# Revit family: EFF1_63_UN_Spot_ETK
name_source: partatom
category: Lighting Fixtures
units: mm (PartAtom-declared; Revit-internal decimal feet)

## family parameters
Always vertical = Yes
Cut with Voids When Loaded = Yes
Light Source = No
OmniClass Number = 23.80.70.11.14.11
OmniClass Title = Downlights
Part Type = Normal
Room Calculation Point = Yes
Round Connector Dimension = Use Diameter
Shared = No
Work Plane-Based = No

## types (12) — shared parameters
Assembly Code = 63.0
Bundle = 40°
IfcExportAs = IfcLightFixtureType
IfcExportType = USERDEFINED
Lamp = LED
Manufacturer = ETK licht B.V.
Material = RAL 9003
Model = EFF.1
URL = https://www.etk.nl
Voltage = 230 V

## per-type parameters (varying)
| type | Apparent Load | Light Source | Wattage Comments |
| EFF.1300.15 - 12W / 1500lm / 3000K | 12 VA | EFF.1 - Lightsource : EFF.1300.15 - 12W / 1500lm / 3000K | 12W |
| EFF.1500.15 - 12W / 1550lm / 4000K | 12 VA | EFF.1 - Lightsource : EFF.1500.15 - 12W / 1550lm / 4000K | 12W |
| EFF.1700.15 - 19W / 2400lm / 3000K | 12 VA | EFF.1 - Lightsource : EFF.1700.15 - 19W / 2400lm / 3000K | 12W |
| EFF.1900.15 - 19W / 2500lm / 4000K | 19 VA | EFF.1 - Lightsource : EFF.1900.15 - 19W / 2500lm / 4000K | 19W |
| EFF.1920.15 - 31W / 3550lm / 3000K | 31 VA | EFF.1 - Lightsource : EFF.1920.15 - 31W / 3550lm / 3000K | 31W |
| EFF.1940.15 - 31W / 3650lm / 4000K | 31 VA | EFF.1 - Lightsource : EFF.1940.15 - 31W / 3650lm / 4000K | 31W |
| EFF.1303.15 - 12W / 1500lm / 3000K | 12 VA | EFF.1 - Lightsource : EFF.1303.15 - 12W / 1500lm / 3000K | 12W |
| EFF.1503.15 - 12W / 1550lm / 4000K | 12 VA | EFF.1 - Lightsource : EFF.1503.15 - 12W / 1550lm / 4000K | 12W |
| EFF.1703.15 - 19W / 2400lm / 3000K | 12 VA | EFF.1 - Lightsource : EFF.1703.15 - 19W / 2400lm / 3000K | 12W |
| EFF.1903.15 - 19W / 2500lm / 4000K | 19 VA | EFF.1 - Lightsource : EFF.1903.15 - 19W / 2500lm / 4000K | 19W |
| EFF.1923.15 - 31W / 3550lm / 3000K | 31 VA | EFF.1 - Lightsource : EFF.1923.15 - 31W / 3550lm / 3000K | 31W |
| EFF.1943.15 - 31W / 3650lm / 4000K | 31 VA | EFF.1 - Lightsource : EFF.1943.15 - 31W / 3650lm / 4000K | 31W |

## geometry (parser evidence)
native form markers: Sweep x5
no freeform markers — native parametric forms only
